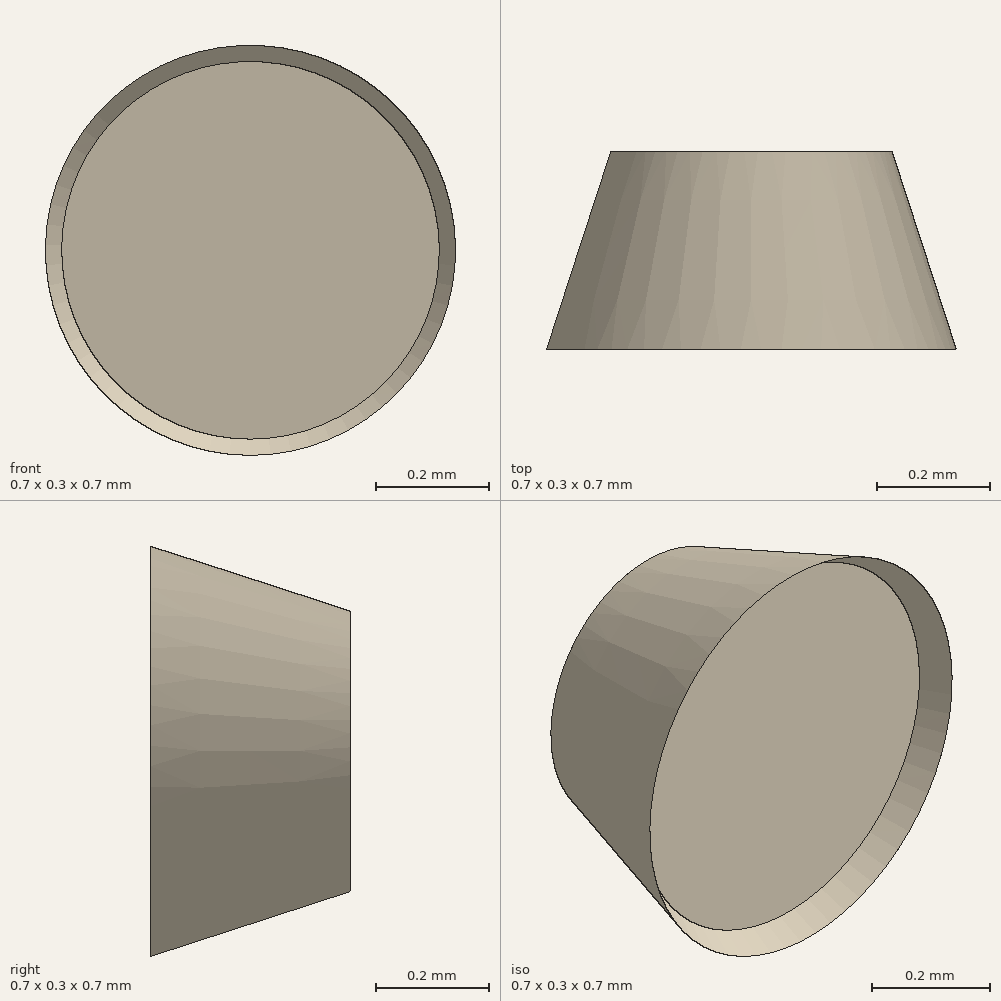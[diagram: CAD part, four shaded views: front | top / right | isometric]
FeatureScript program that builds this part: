
annotation { "Feature Type Name" : "Feature", "Feature Type Description" : "" }
export const myFeature = defineFeature(function(context is Context, id is Id, definition is map)
    precondition{}
    {
        {
            var Q0;
            Q0=qCreatedBy(makeId("Right.planeOp"),FACE);
            var sketch = newSketch(context, id + "F0", { "sketchPlane" : qUnion([Q0])});
            skLineSegment(sketch, "E0.bottom", {"start": v(0.05, 0) * mm, "end": v(0.3, 0) * mm});
            skLineSegment(sketch, "E1", {"start": v(0.35, 0.25) * mm, "end": v(0.3, 0.25) * mm});
            skLineSegment(sketch, "E2", {"start": v(0.3, 0.25) * mm, "end": v(0.3, 0) * mm});
            skLineSegment(sketch, "E3", {"start": v(0, 0.36) * mm, "end": v(0.05, 0.34) * mm});
            skLineSegment(sketch, "E4", {"start": v(0.05, 0.34) * mm, "end": v(0.05, 0) * mm});
            skLineSegment(sketch, "E5", {"start": v(0.35, 0.25) * mm, "end": v(0, 0.36) * mm});
            skSolve(sketch);
        }
        {
            var Q0;
            Q0 = qSketchRegion(id + "F0", true);
            var Q1;
            Q1=sQuery(id+"F0.wireOp",EDGE,"E0.bottom");
            revolve(context, id + "F1", {"entities" : qUnion([Q0]), "axis" : qUnion([Q1]), "revolveType" : RevolveType.FULL});
        }
    });
